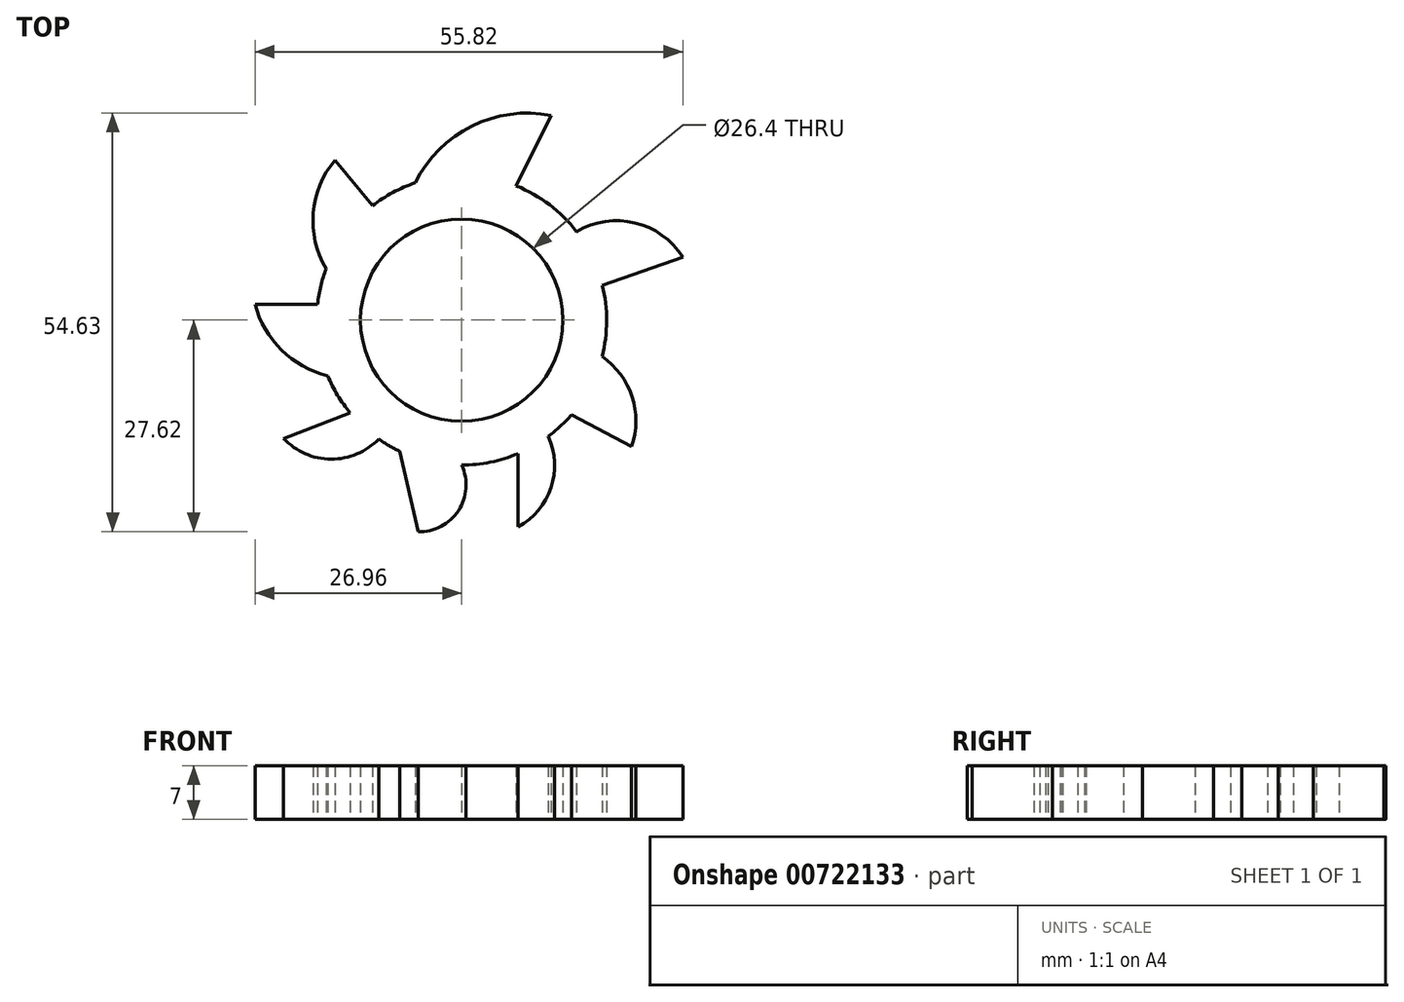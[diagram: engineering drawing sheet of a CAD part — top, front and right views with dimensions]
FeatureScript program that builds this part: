
annotation { "Feature Type Name" : "Feature", "Feature Type Description" : "" }
export const myFeature = defineFeature(function(context is Context, id is Id, definition is map)
    precondition{}
    {
        {
            var Q0;
            Q0=qCreatedBy(makeId("Top.planeOp"),FACE);
            var sketch = newSketch(context, id + "F0", { "sketchPlane" : qUnion([Q0])});
            skCircle(sketch, "E0", {"center": v(0, 0) * mm, "radius": 11.2 * mm});
            skCircle(sketch, "E1", {"center": v(0, 0) * mm, "radius": 13.2 * mm});
            skCircle(sketch, "E2", {"center": v(0, 0) * mm, "radius": 18.91 * mm});
            skArc(sketch, "E3", {"start": v(11.68, 26.71) * mm, "mid": v(1.33, 25.3) * mm, "end": v(-6.06, 17.92) * mm});
            skLineSegment(sketch, "E4", {"start": v(11.68, 26.71) * mm, "end": v(7.13, 17.52) * mm});
            skArc(sketch, "E5", {"start": v(28.86, 8.19) * mm, "mid": v(22.6, 12.69) * mm, "end": v(14.99, 11.54) * mm});
            skLineSegment(sketch, "E6", {"start": v(28.86, 8.19) * mm, "end": v(18.36, 4.54) * mm});
            skArc(sketch, "E7", {"start": v(22.15, -16.51) * mm, "mid": v(22.23, -9.97) * mm, "end": v(18.31, -4.74) * mm});
            skLineSegment(sketch, "E8", {"start": v(14.35, -12.33) * mm, "end": v(22.15, -16.51) * mm});
            skArc(sketch, "E9", {"start": v(-16.52, 20.88) * mm, "mid": v(-19.36, 13.99) * mm, "end": v(-17.68, 6.72) * mm});
            skLineSegment(sketch, "E10", {"start": v(-16.52, 20.88) * mm, "end": v(-11.62, 14.92) * mm});
            skArc(sketch, "E11", {"start": v(-26.96, 2.09) * mm, "mid": v(-23.51, -3.9) * mm, "end": v(-17.47, -7.25) * mm});
            skLineSegment(sketch, "E12", {"start": v(-26.96, 2.09) * mm, "end": v(-18.8, 2.09) * mm});
            skArc(sketch, "E13", {"start": v(-23.22, -15.44) * mm, "mid": v(-17.04, -18.14) * mm, "end": v(-10.82, -15.51) * mm});
            skLineSegment(sketch, "E14", {"start": v(-23.22, -15.44) * mm, "end": v(-14.54, -12.1) * mm});
            skLineSegment(sketch, "E15", {"start": v(7.38, -26.98) * mm, "end": v(7.38, -17.41) * mm});
            skArc(sketch, "E16", {"start": v(-5.68, -27.62) * mm, "mid": v(-0.41, -24.85) * mm, "end": v(0, -18.91) * mm});
            skLineSegment(sketch, "E17", {"start": v(-5.68, -27.62) * mm, "end": v(-8.09, -17.1) * mm});
            skArc(sketch, "E18", {"start": v(7.38, -26.98) * mm, "mid": v(11.67, -21.85) * mm, "end": v(11.3, -15.16) * mm});
            skSolve(sketch);
        }
        {
            var Q0;
            Q0 = qSketchRegion(id + "F0", true);
            extrude(context, id + "F1", {"entities" : qUnion([Q0]), "depth" : 7 * mm, "offsetDistance" : 25 * mm});
        }
    });
